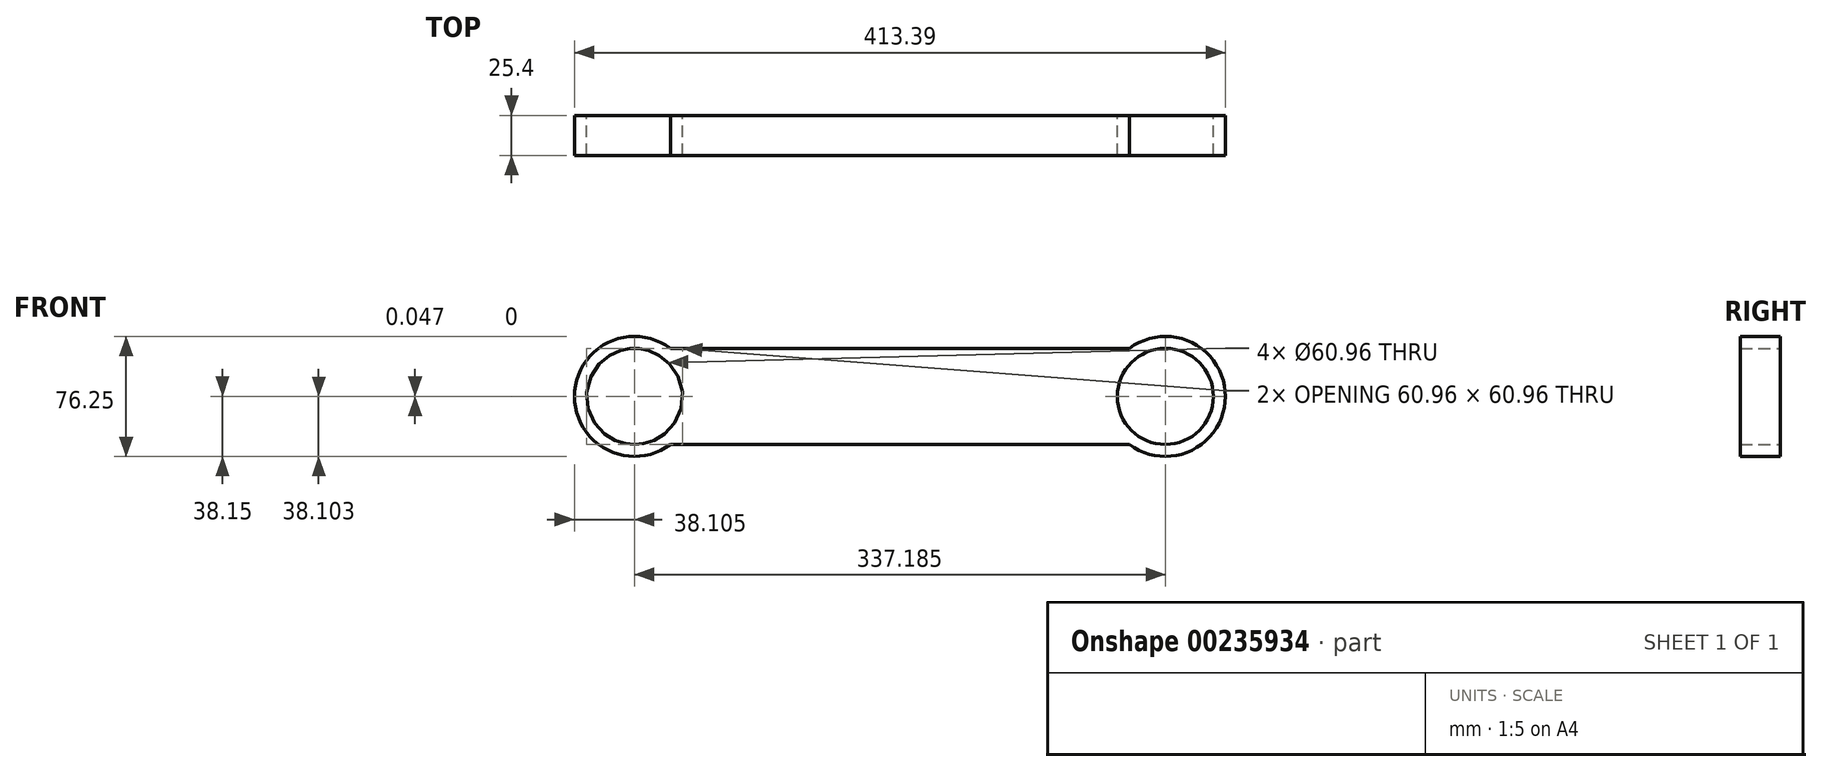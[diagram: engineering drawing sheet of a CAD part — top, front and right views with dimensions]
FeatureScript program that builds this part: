
annotation { "Feature Type Name" : "Feature", "Feature Type Description" : "" }
export const myFeature = defineFeature(function(context is Context, id is Id, definition is map)
    precondition{}
    {
        {
            var Q0;
            Q0=qCreatedBy(makeId("Front.planeOp"),FACE);
            var sketch = newSketch(context, id + "F0", { "sketchPlane" : qUnion([Q0])});
            skCircle(sketch, "E0", {"center": v(-230.5, 0) * mm, "radius": 30.48 * mm});
            skCircle(sketch, "E1", {"center": v(106.68, -0.05) * mm, "radius": 30.48 * mm});
            skLineSegment(sketch, "E2", {"start": v(-207.64, 30.48) * mm, "end": v(83.82, 30.44) * mm});
            skLineSegment(sketch, "E3", {"start": v(-230.5, -30.48) * mm, "end": v(-230.5, -30.48) * mm});
            skArc(sketch, "E4", {"start": v(-207.64, 30.48) * mm, "mid": v(-268.6, 0) * mm, "end": v(-207.64, -30.48) * mm});
            skArc(sketch, "E5", {"start": v(83.7, -30.44) * mm, "mid": v(144.78, -0.13) * mm, "end": v(83.82, 30.44) * mm});
            skPoint(sketch, "E6.orphan", {"position": v(-230.5, 30.48) * mm});
            skLineSegment(sketch, "E7.trimOffspring", {"start": v(-207.64, -30.48) * mm, "end": v(83.7, -30.44) * mm});
            skPoint(sketch, "E8.start.orphan", {"position": v(106.68, -30.53) * mm});
            skSolve(sketch);
        }
        {
            var Q0;
            Q0=makeQuery(id+"F0.imprint","IMPRINT",FACE,{"disambiguationData":[TD([[makeQuery(id+"F0.imprint","IMPRINT",EDGE,{"derivedFrom":sQuery(id+"F0.wireOp",EDGE,"E1")}),-1.0]])]});
            extrude(context, id + "F1", {"entities" : qUnion([Q0]), "depth" : 25.4 * mm, "offsetDistance" : 25.4 * mm});
        }
        {
            var Q0;
            Q0=makeQuery(id+"F0.imprint","IMPRINT",FACE,{"disambiguationData":[TD([[makeQuery(id+"F0.imprint","IMPRINT",EDGE,{"derivedFrom":sQuery(id+"F0.wireOp",EDGE,"E1")}),-1.0]])]});
            extrude(context, id + "F2", {"entities" : qUnion([Q0]), "depth" : 25.4 * mm});
        }
    });
